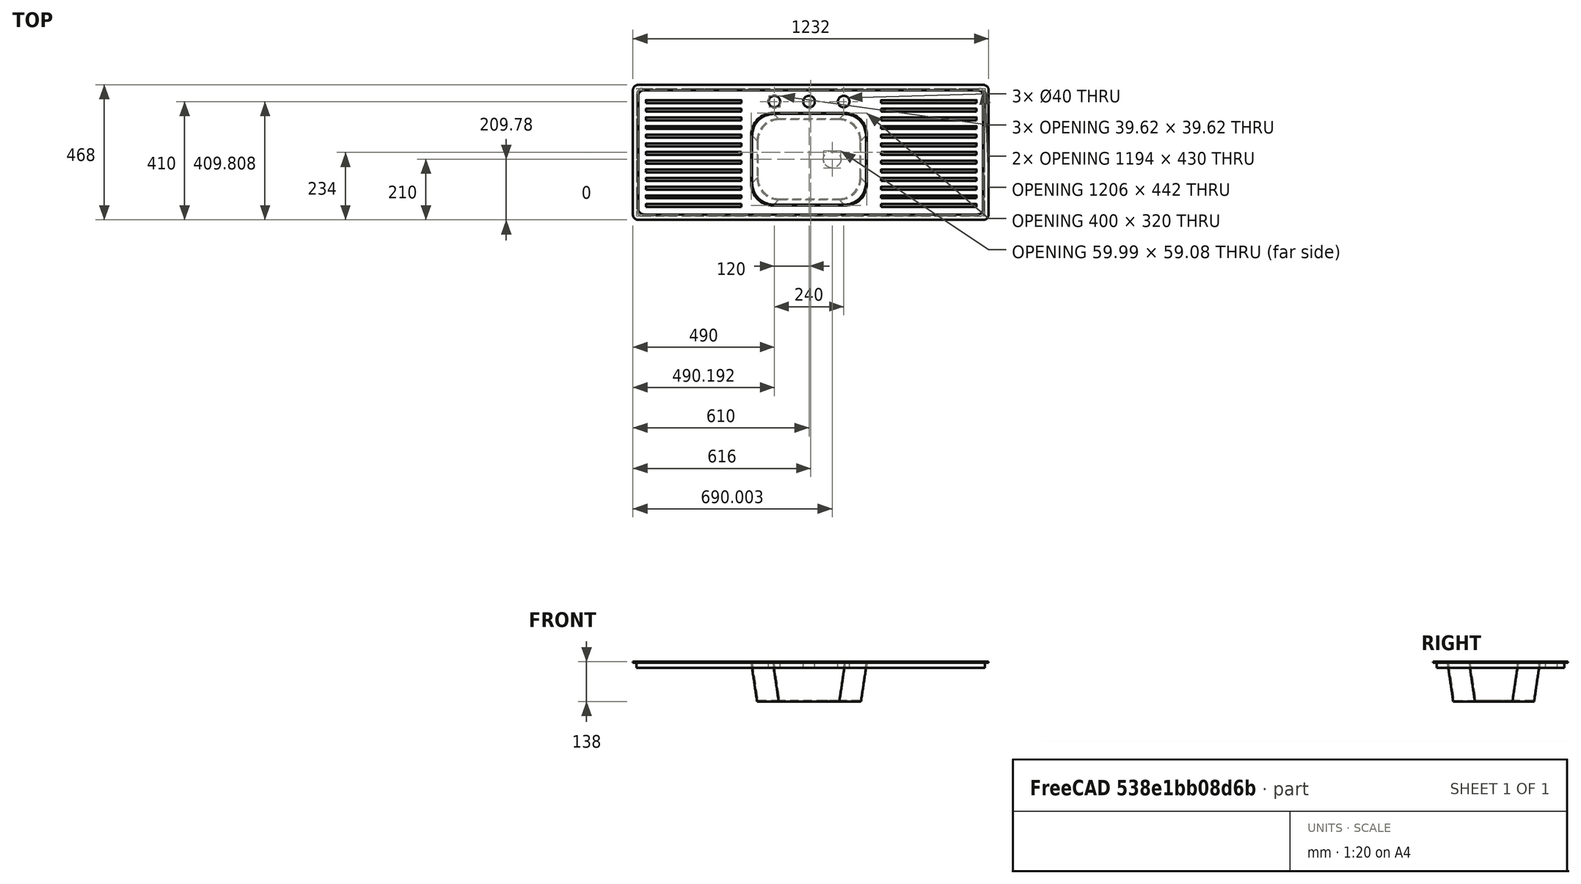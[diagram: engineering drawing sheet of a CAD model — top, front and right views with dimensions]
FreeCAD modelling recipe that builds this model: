
FCSTD DOCUMENT
Label: kitchen_sink_single_pressed_stainless_steel
objects: Sketcher::SketchObject×9, Part::Cut×3, Part::Feature×3, App::DocumentObjectGroup×3, PartDesign::Pad×2, Part::Sweep×2, Part::MultiFuse×2, Part::FeaturePython×2, PartDesign::Pocket×1, Part::Extrusion×1, Part::Cylinder×1, Part::Box×1, Part::Fillet×1
note: 30 computed .brp shape members not serialized (recipe doc carries the construction recipe); baked Part::Feature solids carry a one-line shape summary decoded from their .brp

FEATURE [Sketcher::SketchObject] Sketch
  sketch-geometry (20):
    g0: LineSegment StartX=19 StartY=0 StartZ=0 EndX=1213 EndY=0 EndZ=0
    g1: LineSegment StartX=1232 StartY=19 StartZ=0 EndX=1232 EndY=449 EndZ=0
    g2: LineSegment StartX=1213 StartY=468 StartZ=0 EndX=19 EndY=468 EndZ=0
    g3: LineSegment StartX=0 StartY=449 StartZ=0 EndX=0 EndY=19 EndZ=0
    g4: LineSegment [constr] StartX=0 StartY=19 StartZ=0 EndX=19 EndY=19 EndZ=0
    g5: LineSegment [constr] StartX=19 StartY=0 StartZ=0 EndX=19 EndY=19 EndZ=0
    g6: LineSegment [constr] StartX=1232 StartY=449 StartZ=0 EndX=1213 EndY=449 EndZ=0
    g7: LineSegment [constr] StartX=1213 StartY=468 StartZ=0 EndX=1213 EndY=449 EndZ=0
    g8: ArcOfCircle CenterX=19 CenterY=19 CenterZ=0 NormalX=0 NormalY=0 NormalZ=1 Radius=19 StartAngle=3.14159 EndAngle=4.71239
    g9: ArcOfCircle CenterX=1213 CenterY=19 CenterZ=0 NormalX=0 NormalY=0 NormalZ=1 Radius=19 StartAngle=4.71239 EndAngle=6.28319
    g10: ArcOfCircle CenterX=1213 CenterY=449 CenterZ=0 NormalX=0 NormalY=0 NormalZ=1 Radius=19 StartAngle=0 EndAngle=1.5708
    g11: ArcOfCircle CenterX=19 CenterY=449 CenterZ=0 NormalX=0 NormalY=0 NormalZ=1 Radius=19 StartAngle=1.5708 EndAngle=3.14159
    g12: LineSegment StartX=19 StartY=430 StartZ=0 EndX=19 EndY=38 EndZ=0
    g13: LineSegment StartX=38 StartY=19 StartZ=0 EndX=1194 EndY=19 EndZ=0
    g14: LineSegment StartX=1213 StartY=430 StartZ=0 EndX=1213 EndY=38 EndZ=0
    g15: ArcOfCircle CenterX=38 CenterY=430 CenterZ=0 NormalX=0 NormalY=0 NormalZ=1 Radius=19 StartAngle=1.57056 EndAngle=3.14159
    g16: LineSegment StartX=38.0044 StartY=449 StartZ=0 EndX=1194 EndY=449 EndZ=0
    g17: ArcOfCircle CenterX=38 CenterY=38 CenterZ=0 NormalX=0 NormalY=0 NormalZ=1 Radius=19 StartAngle=3.14159 EndAngle=4.71239
    g18: ArcOfCircle CenterX=1194 CenterY=430 CenterZ=0 NormalX=0 NormalY=0 NormalZ=1 Radius=19 StartAngle=3.15789e-07 EndAngle=1.5708
    g19: ArcOfCircle CenterX=1194 CenterY=38 CenterZ=0 NormalX=0 NormalY=0 NormalZ=1 Radius=19 StartAngle=4.71239 EndAngle=6.28319
  constraints (69):
    c: Horizontal(g0)
    c: Horizontal(g2)
    c: Vertical(g1)
    c: Vertical(g3)
    c: DistanceY(g2,g0) = -468
    c: DistanceX(g3,g1) = 1232
    c: Equal(g2,g0)
    c: Equal(g1,g3)
    c: DistanceY(g3,g1) = 0
    c: DistanceX(g0,g2) = 0
    c: DistanceY(g0) = 0
    c: DistanceX(g3) = 0
    c: Coincident(g4,g3)
    c: Horizontal(g4)
    c: Coincident(g5,g0)
    c: Vertical(g5)
    c: Coincident(g5,g4)
    c: Equal(g4,g5)
    c: Coincident(g6,g1)
    c: Horizontal(g6)
    c: Coincident(g7,g2)
    c: Vertical(g7)
    c: Coincident(g7,g6)
    c: Equal(g7,g6)
    c: Equal(g6,g5)
    c: Coincident(g8,g4)
    c: Coincident(g8,g3)
    c: Coincident(g8,g0)
    c: Radius(g8) = 19
    c: Coincident(g9,g1)
    c: Coincident(g9,g0)
    c: Radius(g9) = 19
    c: Coincident(g10,g6)
    c: Coincident(g10,g2)
    c: Coincident(g10,g1)
    c: Coincident(g11,g2)
    c: Radius(g11) = 19
    c: Vertical(g12)
    c: Horizontal(g13)
    c: Vertical(g14)
    c: DistanceX(g3,g2) = 19
    c: DistanceY(g12,g3) = 19
    c: DistanceX(g12,g3) = -19
    c: Coincident(g15,g12)
    c: Coincident(g3,g11)
    c: Coincident(g16,g15)
    c: Horizontal(g16)
    c: DistanceX(g2,g16) = -19
    c: DistanceY(g1,g14) = -19
    c: DistanceX(g1,g14) = -19
    c: DistanceX(g13,g0) = 19
    c: DistanceY(g14,g1) = -19
    c: DistanceY(g0,g13) = 19
    c: DistanceX(g0,g13) = 19
    c: DistanceY(g3,g12) = 19
    c: Coincident(g17,g13)
    c: Coincident(g17,g12)
    c: Coincident(g18,g16)
    c: Coincident(g18,g14)
    c: DistanceX(g15,g2) = -19.0044
    c: DistanceY(g15,g2) = 19
    c: Coincident(g19,g14)
    c: Coincident(g19,g13)
    c: Tangent(g18,g14)
    c: Tangent(g16,g18)
    c: Radius(g19) = 19
    c: Radius(g18) = 19
    c: Radius(g17) = 19
    c: Radius(g15) = 19
FEATURE [Sketcher::SketchObject] Sketch001
  Placement = pos=(0,0,-15) rot=(0,0,1;0rad)
  sketch-geometry (8):
    g0: LineSegment StartX=410 StartY=295 StartZ=0 EndX=410 EndY=125 EndZ=0
    g1: LineSegment StartX=485 StartY=50 StartZ=0 EndX=735 EndY=50 EndZ=0
    g2: LineSegment StartX=485 StartY=370 StartZ=0 EndX=735 EndY=370 EndZ=0
    g3: LineSegment StartX=810 StartY=295 StartZ=0 EndX=810 EndY=125 EndZ=0
    g4: ArcOfCircle CenterX=485 CenterY=295 CenterZ=0 NormalX=0 NormalY=0 NormalZ=1 Radius=75 StartAngle=1.5708 EndAngle=3.14159
    g5: ArcOfCircle CenterX=485 CenterY=125 CenterZ=0 NormalX=0 NormalY=0 NormalZ=1 Radius=75 StartAngle=3.14159 EndAngle=4.71239
    g6: ArcOfCircle CenterX=735 CenterY=125 CenterZ=0 NormalX=0 NormalY=0 NormalZ=1 Radius=75 StartAngle=4.71239 EndAngle=6.28319
    g7: ArcOfCircle CenterX=735 CenterY=295 CenterZ=0 NormalX=0 NormalY=0 NormalZ=1 Radius=75 StartAngle=0 EndAngle=1.5708
  constraints (28):
    c: Vertical(g0)
    c: Horizontal(g1)
    c: Horizontal(g2)
    c: Vertical(g3)
    c: Equal(g0,g3)
    c: Equal(g2,g1)
    c: DistanceY(g2,g1) = -320
    c: DistanceX(g3,g0) = -400
    c: DistanceX(g0) = 410
    c: DistanceY(g1) = 50
    c: DistanceX(g1,g2) = 0
    c: DistanceX(g1,g3) = 75
    c: DistanceY(g1,g3) = 75
    c: DistanceY(g3,g2) = 75
    c: DistanceY(g0,g3) = 0
    c: DistanceX(g0,g2) = 75
    c: Coincident(g4,g2)
    c: Coincident(g4,g0)
    c: Coincident(g5,g1)
    c: Coincident(g5,g0)
    c: Coincident(g6,g3)
    c: Coincident(g7,g2)
    c: Coincident(g7,g3)
    c: Radius(g4) = 75
    c: Radius(g7) = 75
    c: Radius(g6) = 75
    c: Radius(g5) = 75
    c: Coincident(g1,g6)
FEATURE [Sketcher::SketchObject] Sketch002
  Placement = pos=(0,0,-150) rot=(0,0,1;0rad)
  sketch-geometry (8):
    g0: LineSegment StartX=430 StartY=275 StartZ=0 EndX=430 EndY=145 EndZ=0
    g1: LineSegment StartX=505 StartY=70 StartZ=0 EndX=715 EndY=70 EndZ=0
    g2: LineSegment StartX=505 StartY=350 StartZ=0 EndX=715 EndY=350 EndZ=0
    g3: LineSegment StartX=790 StartY=275 StartZ=0 EndX=790 EndY=145 EndZ=0
    g4: ArcOfCircle CenterX=505 CenterY=275 CenterZ=0 NormalX=0 NormalY=0 NormalZ=1 Radius=75 StartAngle=1.5708 EndAngle=3.14159
    g5: ArcOfCircle CenterX=505 CenterY=145 CenterZ=0 NormalX=0 NormalY=0 NormalZ=1 Radius=75 StartAngle=3.14159 EndAngle=4.71239
    g6: ArcOfCircle CenterX=715 CenterY=145 CenterZ=0 NormalX=0 NormalY=0 NormalZ=1 Radius=75 StartAngle=4.71239 EndAngle=6.28319
    g7: ArcOfCircle CenterX=715 CenterY=275 CenterZ=0 NormalX=0 NormalY=0 NormalZ=1 Radius=75 StartAngle=0 EndAngle=1.5708
  constraints (28):
    c: Vertical(g0)
    c: Horizontal(g1)
    c: Horizontal(g2)
    c: Vertical(g3)
    c: Equal(g0,g3)
    c: Equal(g2,g1)
    c: DistanceY(g2,g1) = -280
    c: DistanceX(g3,g0) = -360
    c: DistanceX(g0) = 430
    c: DistanceY(g1) = 70
    c: DistanceX(g1,g2) = 0
    c: DistanceX(g1,g3) = 75
    c: DistanceY(g1,g3) = 75
    c: DistanceY(g3,g2) = 75
    c: DistanceY(g0,g3) = 0
    c: DistanceX(g0,g2) = 75
    c: Coincident(g4,g2)
    c: Coincident(g4,g0)
    c: Coincident(g5,g1)
    c: Coincident(g5,g0)
    c: Coincident(g6,g3)
    c: Coincident(g7,g2)
    c: Coincident(g7,g3)
    c: Radius(g4) = 75
    c: Radius(g7) = 75
    c: Radius(g6) = 75
    c: Radius(g5) = 75
    c: Coincident(g1,g6)
FEATURE [PartDesign::Pad] Pad
  FaceName = No face selected
  Length = 3
  Length2 = 100
  Reversed = true
  Sketch = -> Sketch
  Type = 0
FEATURE [Sketcher::SketchObject] Sketch003
  ExternalGeometry = -> [Pad]
  Placement = pos=(0,0,-3) rot=(1,0,0;3.14159rad)
  Support = -> Pad [Face18]
  sketch-geometry (8):
    g0: LineSegment StartX=32.0044 StartY=-455 StartZ=0 EndX=1200 EndY=-455 EndZ=0
    g1: LineSegment StartX=13 StartY=-436 StartZ=0 EndX=13 EndY=-32 EndZ=0
    g2: LineSegment StartX=32 StartY=-13 StartZ=0 EndX=1200 EndY=-13 EndZ=0
    g3: LineSegment StartX=1219 StartY=-32 StartZ=0 EndX=1219 EndY=-436 EndZ=0
    g4: ArcOfCircle CenterX=32 CenterY=-436 CenterZ=0 NormalX=0 NormalY=0 NormalZ=1 Radius=19 StartAngle=3.14159 EndAngle=4.71262
    g5: ArcOfCircle CenterX=32 CenterY=-32 CenterZ=0 NormalX=0 NormalY=0 NormalZ=1 Radius=19 StartAngle=1.5708 EndAngle=3.14159
    g6: ArcOfCircle CenterX=1200 CenterY=-32 CenterZ=0 NormalX=0 NormalY=0 NormalZ=1 Radius=19 StartAngle=0 EndAngle=1.5708
    g7: ArcOfCircle CenterX=1200 CenterY=-436 CenterZ=0 NormalX=0 NormalY=0 NormalZ=1 Radius=19 StartAngle=4.71239 EndAngle=6.28319
  constraints (28):
    c: Horizontal(g0)
    c: DistanceY(g-5,g0) = -6
    c: Vertical(g1)
    c: DistanceX(g-3,g1) = -6
    c: DistanceY(g-3,g1) = -6
    c: DistanceX(g-5,g0) = -6
    c: DistanceY(g1,g-3) = -6
    c: Horizontal(g2)
    c: DistanceX(g2,g-6) = 6
    c: DistanceY(g-6,g2) = 6
    c: DistanceX(g2,g-6) = -6
    c: Vertical(g3)
    c: DistanceX(g3,g-4) = -6
    c: DistanceY(g3,g-4) = -6
    c: DistanceY(g3,g-4) = 6
    c: DistanceX(g-5,g0) = 6
    c: Coincident(g4,g1)
    c: Coincident(g4,g0)
    c: Coincident(g5,g1)
    c: Coincident(g5,g2)
    c: Radius(g5) = 19
    c: Coincident(g6,g2)
    c: Coincident(g6,g3)
    c: Radius(g6) = 19
    c: Coincident(g7,g3)
    c: Coincident(g7,g0)
    c: Radius(g7) = 19
    c: Radius(g4) = 19
FEATURE [PartDesign::Pad] Pad001
  FaceName = No face selected
  Length = 18
  Length2 = 100
  Sketch = -> Sketch003
  Type = 0
FEATURE [Sketcher::SketchObject] Sketch004
  Placement = pos=(0,0,-15) rot=(0,0,1;0rad)
  sketch-geometry (8):
    g0: LineSegment StartX=413 StartY=292 StartZ=0 EndX=413 EndY=128 EndZ=0
    g1: LineSegment StartX=488 StartY=53 StartZ=0 EndX=732 EndY=53 EndZ=0
    g2: LineSegment StartX=488 StartY=367 StartZ=0 EndX=732 EndY=367 EndZ=0
    g3: LineSegment StartX=807 StartY=292 StartZ=0 EndX=807 EndY=128 EndZ=0
    g4: ArcOfCircle CenterX=488 CenterY=292 CenterZ=0 NormalX=0 NormalY=0 NormalZ=1 Radius=75 StartAngle=1.5708 EndAngle=3.14159
    g5: ArcOfCircle CenterX=488 CenterY=128 CenterZ=0 NormalX=0 NormalY=0 NormalZ=1 Radius=75 StartAngle=3.14159 EndAngle=4.71239
    g6: ArcOfCircle CenterX=732 CenterY=128 CenterZ=0 NormalX=0 NormalY=0 NormalZ=1 Radius=75 StartAngle=4.71239 EndAngle=6.28319
    g7: ArcOfCircle CenterX=732 CenterY=292 CenterZ=0 NormalX=0 NormalY=0 NormalZ=1 Radius=75 StartAngle=0 EndAngle=1.5708
  constraints (28):
    c: Vertical(g0)
    c: Horizontal(g1)
    c: Horizontal(g2)
    c: Vertical(g3)
    c: Equal(g0,g3)
    c: Equal(g2,g1)
    c: DistanceY(g2,g1) = -314
    c: DistanceX(g3,g0) = -394
    c: DistanceX(g0) = 413
    c: DistanceY(g1) = 53
    c: DistanceX(g1,g2) = 0
    c: DistanceX(g1,g3) = 75
    c: DistanceY(g1,g3) = 75
    c: DistanceY(g3,g2) = 75
    c: DistanceY(g0,g3) = 0
    c: DistanceX(g0,g2) = 75
    c: Coincident(g4,g2)
    c: Coincident(g4,g0)
    c: Coincident(g5,g1)
    c: Coincident(g5,g0)
    c: Coincident(g6,g3)
    c: Coincident(g7,g2)
    c: Coincident(g7,g3)
    c: Radius(g4) = 75
    c: Radius(g7) = 75
    c: Radius(g6) = 75
    c: Radius(g5) = 75
    c: Coincident(g1,g6)
FEATURE [Sketcher::SketchObject] Sketch005
  Placement = pos=(0,0,-147) rot=(0,0,1;0rad)
  sketch-geometry (8):
    g0: LineSegment StartX=433 StartY=272 StartZ=0 EndX=433 EndY=148 EndZ=0
    g1: LineSegment StartX=508 StartY=73 StartZ=0 EndX=712 EndY=73 EndZ=0
    g2: LineSegment StartX=508 StartY=347 StartZ=0 EndX=712 EndY=347 EndZ=0
    g3: LineSegment StartX=787 StartY=272 StartZ=0 EndX=787 EndY=148 EndZ=0
    g4: ArcOfCircle CenterX=508 CenterY=272 CenterZ=0 NormalX=0 NormalY=0 NormalZ=1 Radius=75 StartAngle=1.5708 EndAngle=3.14159
    g5: ArcOfCircle CenterX=508 CenterY=148 CenterZ=0 NormalX=0 NormalY=0 NormalZ=1 Radius=75 StartAngle=3.14159 EndAngle=4.71239
    g6: ArcOfCircle CenterX=712 CenterY=148 CenterZ=0 NormalX=0 NormalY=0 NormalZ=1 Radius=75 StartAngle=4.71239 EndAngle=6.28319
    g7: ArcOfCircle CenterX=712 CenterY=272 CenterZ=0 NormalX=0 NormalY=0 NormalZ=1 Radius=75 StartAngle=0 EndAngle=1.5708
  constraints (28):
    c: Vertical(g0)
    c: Horizontal(g1)
    c: Horizontal(g2)
    c: Vertical(g3)
    c: Equal(g0,g3)
    c: Equal(g2,g1)
    c: DistanceY(g2,g1) = -274
    c: DistanceX(g3,g0) = -354
    c: DistanceX(g0) = 433
    c: DistanceY(g1) = 73
    c: DistanceX(g1,g2) = 0
    c: DistanceX(g1,g3) = 75
    c: DistanceY(g1,g3) = 75
    c: DistanceY(g3,g2) = 75
    c: DistanceY(g0,g3) = 0
    c: DistanceX(g0,g2) = 75
    c: Coincident(g4,g2)
    c: Coincident(g4,g0)
    c: Coincident(g5,g1)
    c: Coincident(g5,g0)
    c: Coincident(g6,g3)
    c: Coincident(g7,g2)
    c: Coincident(g7,g3)
    c: Radius(g4) = 75
    c: Radius(g7) = 75
    c: Radius(g6) = 75
    c: Radius(g5) = 75
    c: Coincident(g1,g6)
FEATURE [Sketcher::SketchObject] Sketch006
  Placement = pos=(0,210,0) rot=(-1,0,0;4.71239rad)
  sketch-geometry (1):
    g0: LineSegment StartX=610 StartY=-15 StartZ=0 EndX=610 EndY=-147 EndZ=0
  constraints (4):
    c: Vertical(g0)
    c: DistanceX(g0) = 610
    c: DistanceY(g0) = -147
    c: DistanceY(g0) = -15
FEATURE [Part::Sweep] Sweep
  Frenet = false
  Placement = pos=(0,0,12) rot=(0,0,1;0rad)
  Sections = -> [Sketch004,Sketch005]
  Solid = true
  Spine = -> Sketch006 [Edge1]
  Transition = 1
FEATURE [Sketcher::SketchObject] Sketch007
  Placement = pos=(0,0,-3) rot=(0,0,1;0rad)
  Support = -> Pad001 [Face27]
  sketch-geometry (8):
    g0: LineSegment StartX=410 StartY=295 StartZ=0 EndX=410 EndY=125 EndZ=0
    g1: LineSegment StartX=485 StartY=50 StartZ=0 EndX=735 EndY=50 EndZ=0
    g2: LineSegment StartX=485 StartY=370 StartZ=0 EndX=735 EndY=370 EndZ=0
    g3: LineSegment StartX=810 StartY=295 StartZ=0 EndX=810 EndY=125 EndZ=0
    g4: ArcOfCircle CenterX=485 CenterY=295 CenterZ=0 NormalX=0 NormalY=0 NormalZ=1 Radius=75 StartAngle=1.5708 EndAngle=3.14159
    g5: ArcOfCircle CenterX=485 CenterY=125 CenterZ=0 NormalX=0 NormalY=0 NormalZ=1 Radius=75 StartAngle=3.14159 EndAngle=4.71239
    g6: ArcOfCircle CenterX=735 CenterY=125 CenterZ=0 NormalX=0 NormalY=0 NormalZ=1 Radius=75 StartAngle=4.71239 EndAngle=6.28319
    g7: ArcOfCircle CenterX=735 CenterY=295 CenterZ=0 NormalX=0 NormalY=0 NormalZ=1 Radius=75 StartAngle=0 EndAngle=1.5708
  constraints (28):
    c: Vertical(g0)
    c: Horizontal(g1)
    c: Horizontal(g2)
    c: Vertical(g3)
    c: Equal(g0,g3)
    c: Equal(g2,g1)
    c: DistanceY(g2,g1) = -320
    c: DistanceX(g3,g0) = -400
    c: DistanceX(g0) = 410
    c: DistanceY(g1) = 50
    c: DistanceX(g1,g2) = 0
    c: DistanceX(g1,g3) = 75
    c: DistanceY(g1,g3) = 75
    c: DistanceY(g3,g2) = 75
    c: DistanceY(g0,g3) = 0
    c: DistanceX(g0,g2) = 75
    c: Coincident(g4,g2)
    c: Coincident(g4,g0)
    c: Coincident(g5,g1)
    c: Coincident(g5,g0)
    c: Coincident(g6,g3)
    c: Coincident(g7,g2)
    c: Coincident(g7,g3)
    c: Radius(g4) = 75
    c: Radius(g7) = 75
    c: Radius(g6) = 75
    c: Radius(g5) = 75
    c: Coincident(g1,g6)
FEATURE [PartDesign::Pocket] Pocket
  Length = 5
  Sketch = -> Sketch007
  Type = 3
FEATURE [Part::Sweep] Sweep001
  Frenet = false
  Placement = pos=(0,0,12) rot=(0,0,1;0rad)
  Sections = -> [Sketch001,Sketch002]
  Solid = true
  Spine = -> Sketch006 [Edge1]
  Transition = 1
FEATURE [Part::Cut] Cut
  Base = -> Sweep001
  Tool = -> Sweep
FEATURE [Part::MultiFuse] Fusion
  Shapes = -> [Pocket,Cut]
FEATURE [Sketcher::SketchObject] Sketch008
  Placement = pos=(0,0,-135) rot=(0,0,1;0rad)
  Support = -> Fusion [Face46]
  sketch-geometry (1):
    g0: Circle CenterX=690 CenterY=210 CenterZ=0 NormalX=0 NormalY=0 NormalZ=1 Radius=30
  constraints (3):
    c: DistanceX(g0) = 690
    c: DistanceY(g0) = 210
    c: Radius(g0) = 30
FEATURE [Part::Feature] Face
  shape: bbox 89.13 x 75.66 x 2.003e-07 mm, 1 faces, 0 solids (baked)
FEATURE [Part::Extrusion] Extrude
  Base = -> Face
  Dir = (0,0,200)
  Placement = pos=(0,0,-15) rot=(0,0,1;0rad)
  Solid = true
FEATURE [Part::Cut] Cut001
  Base = -> Fusion
  Tool = -> Extrude
FEATURE [Part::Cylinder] Cylinder
  Angle = 360
  Height = 50
  Placement = pos=(490,410,-30) rot=(0,0,1;0rad)
  Radius = 20
FEATURE [Part::FeaturePython] Array  # Draft array (typed FeaturePython)
  Angle = 360
  ArrayType = 0
  Axis = (0,0,1)
  Base = -> Cylinder
  Center = (0,0,0)
  IntervalX = (120,0,0)
  IntervalY = (0,1,0)
  NumberPolar = 1
  NumberX = 3
  NumberY = 1
FEATURE [Part::Cut] Cut002
  Base = -> Cut001
  Tool = -> Array
FEATURE [Part::Box] Box
  Height = 2
  Length = 330
  Placement = pos=(45,45,-3) rot=(0,0,1;0rad)
  Width = 10
FEATURE [Part::Feature] Cut002_cs
  shape: bbox 2e-07 x 468 x 21 mm, 0 faces, 0 solids (baked)
FEATURE [Part::Fillet] Fillet
  Base = -> Box
  Edges = 4 edges r=1.99: [Edge2,Edge6,Edge10,Edge12]
FEATURE [Part::FeaturePython] Array001  # Draft array (typed FeaturePython)
  Angle = 360
  ArrayType = 0
  Axis = (0,0,1)
  Base = -> Fillet
  Center = (0,0,0)
  IntervalX = (815,0,0)
  IntervalY = (0,30,0)
  NumberPolar = 1
  NumberX = 2
  NumberY = 13
FEATURE [Part::MultiFuse] Fusion001  label="kitchen_sink_single_stainless_steel_parametric"
  Shapes = -> [Cut002,Array001]
FEATURE [App::DocumentObjectGroup] Group001  label="parametric_components"
  Group = -> [Sketch,Sketch002,Sketch001,Sweep001,Sketch003,Pad001,Pad,Sketch004,Cut,Sketch006,Pocket,Sweep,Sketch007,Sketch005,Fusion,Sketch008,Extrude,Face,Cut001,Cylinder,Array,Cut002,Cut002_cs,Fillet,Box,Array001,Fusion001]
FEATURE [Part::Feature] Fusion001001  label="kitchen_sink_single_stainless_steel_1"
  shape: bbox 1232 x 468 x 138 mm, 293 faces, 2 solids (baked)
FEATURE [App::DocumentObjectGroup] Group002  label="simple_copies"
  Group = -> [Fusion001001]
FEATURE [App::DocumentObjectGroup] Group  label="kitchen_sink_single_stainless_steel"
  Group = -> [Group001,Group002]
